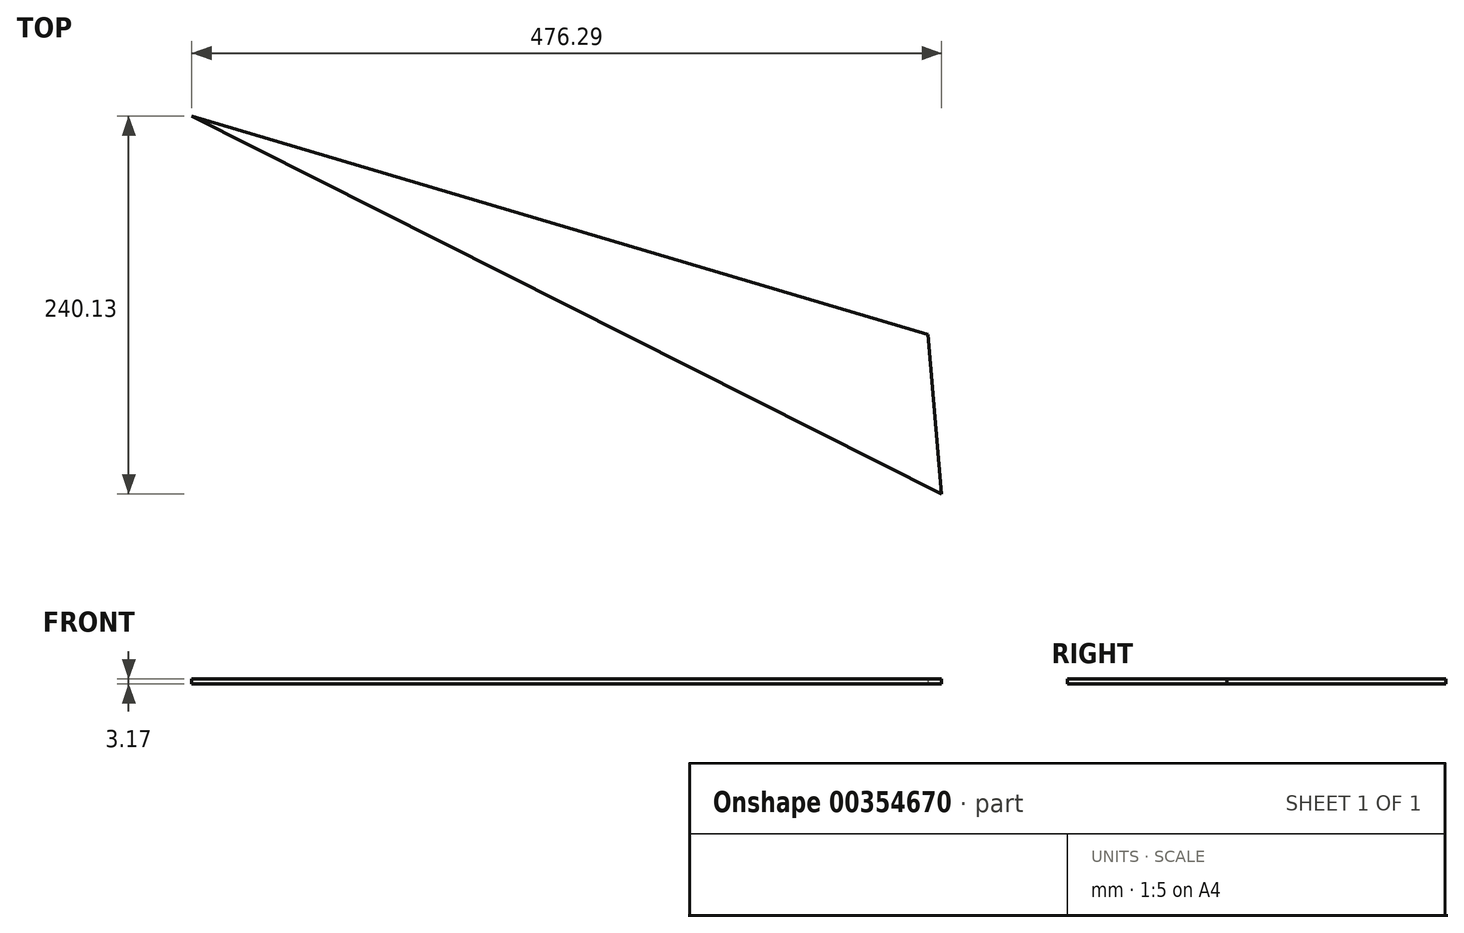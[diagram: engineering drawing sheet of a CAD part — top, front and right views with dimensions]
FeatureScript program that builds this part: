
annotation { "Feature Type Name" : "Feature", "Feature Type Description" : "" }
export const myFeature = defineFeature(function(context is Context, id is Id, definition is map)
    precondition{}
    {
        {
            var Q0;
            Q0=qCreatedBy(makeId("Top.planeOp"),FACE);
            var sketch = newSketch(context, id + "F0", { "sketchPlane" : qUnion([Q0])});
            skLineSegment(sketch, "E0", {"start": v(257.15, -152.74) * mm, "end": v(248.4, -51.52) * mm});
            skLineSegment(sketch, "E1", {"start": v(248.4, -51.52) * mm, "end": v(-219.14, 87.39) * mm});
            skLineSegment(sketch, "E2", {"start": v(-219.14, 87.39) * mm, "end": v(257.15, -152.74) * mm});
            skSolve(sketch);
        }
        {
            var Q0;
            Q0=qSketchRegion(id+"F0",true);
            extrude(context, id + "F1", {"entities" : qUnion([Q0]), "depth" : 3.17 * mm});
        }
    });
